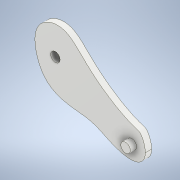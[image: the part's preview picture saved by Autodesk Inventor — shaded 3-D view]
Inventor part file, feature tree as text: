
AUTODESK INVENTOR PART (.ipt)
format: ipt  version: 2022 (Build 260153000, 153)  size: 130,560 bytes
history: native  units: in
note: dims shown in document units (in); Inventor stores cm internally (conversion verified against a paired STEP export)
features: extrude x2, sketch x1
ambient origin geometry x8: Origin, YZ Plane, XZ Plane, XY Plane, X Axis, Y Axis, Z Axis, Center Point
bodies: Solid1 (feature_tree)
feature tree (3):
  sketch  "Sketch2"  dims[d0=0.1969in d1=0.0in d2=0.1969in d3=0.0in d4=0.2953in d5=0.2953in]
  extrude  "Extrusion1"  TaperAngle=0.0deg  [1 undecoded]
  extrude  "Extrusion2"  Depth=0.1969in TaperAngle=0.0deg
note: 1 required parameter value undecoded (feature->parameter linkage not recoverable at this tier; creation-order binding heuristic only, values carry confidence <= 0.55)
